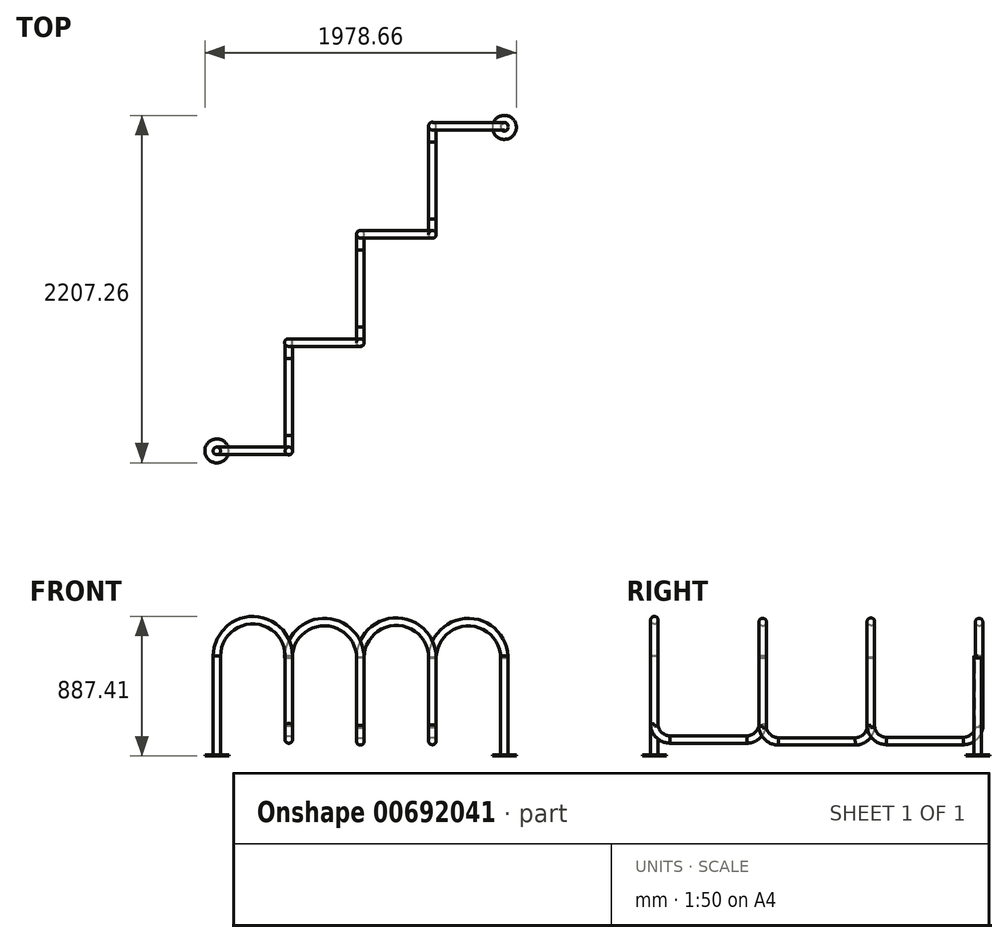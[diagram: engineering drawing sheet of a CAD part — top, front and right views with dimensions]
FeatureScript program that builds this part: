
annotation { "Feature Type Name" : "Feature", "Feature Type Description" : "" }
export const myFeature = defineFeature(function(context is Context, id is Id, definition is map)
    precondition{}
    {
        {
            var Q0;
            Q0=qCreatedBy(makeId("Top.planeOp"),FACE);
            var sketch = newSketch(context, id + "F0", { "sketchPlane" : qUnion([Q0])});
            skCircle(sketch, "E0", {"center": v(0, 0) * mm, "radius": 76.2 * mm});
            skCircle(sketch, "E1", {"center": v(0, 0) * mm, "radius": 23.81 * mm});
            skSolve(sketch);
        }
        {
            var Q0;
            Q0=makeQuery(id+"F0.imprint","IMPRINT",FACE,{"disambiguationData":[TD([[makeQuery(id+"F0.imprint","IMPRINT",EDGE,{"derivedFrom":sQuery(id+"F0.wireOp",EDGE,"E0")}),1.0]])]});
            extrude(context, id + "F1", {"entities" : qUnion([Q0]), "depth" : 6.35 * mm, "offsetDistance" : 25.4 * mm});
        }
        {
            var Q0;
            Q0=makeQuery(id+"F0.imprint","IMPRINT",FACE,{"disambiguationData":[TD([[makeQuery(id+"F0.imprint","IMPRINT",EDGE,{"derivedFrom":sQuery(id+"F0.wireOp",EDGE,"E1")}),1.0]])]});
            extrude(context, id + "F2", {"entities" : qUnion([Q0]), "operationType" : NewBodyOperationType.ADD, "depth" : 635 * mm, "offsetDistance" : 25.4 * mm});
        }
        {
            var Q0;
            Q0=qCreatedBy(makeId("Front.planeOp"),FACE);
            var sketch = newSketch(context, id + "F3", { "sketchPlane" : qUnion([Q0])});
            skArc(sketch, "E2", {"start": v(457.2, 635) * mm, "mid": v(228.6, 863.6) * mm, "end": v(0, 635) * mm});
            skLineSegment(sketch, "E3", {"start": v(0, 0) * mm, "end": v(0, 635) * mm});
            skLineSegment(sketch, "E4", {"start": v(457.2, 635) * mm, "end": v(457.2, 228.6) * mm});
            skLineSegment(sketch, "E5", {"start": v(228.6, 863.6) * mm, "end": v(228.6, 0) * mm, "construction": true});
            skLineSegment(sketch, "E6", {"start": v(228.6, 863.6) * mm, "end": v(951.54, 863.6) * mm, "construction": true});
            skSolve(sketch);
        }
        {
            var Q0;
            Q0=makeQuery(id+"F2.opExtrude","CAP_FACE",FACE,{"disambiguationData":[OSD([sQuery(id+"F0.wireOp",EDGE,"E1")])],"isStart":false});
            var Q1;
            Q1=sQuery(id+"F3.wireOp",EDGE,"E2");
            sweep(context, id + "F4", {"profiles" : qUnion([Q0]), "path" : qUnion([Q1])});
        }
        {
            var Q0;
            Q0=makeQuery(id+"F4.opSweep","CAP_FACE",FACE,{"disambiguationData":[OSD([sQuery(id+"F0.wireOp",EDGE,"E1"),sQuery(id+"F3.wireOp",VERTEX,"E2.start")])],"isStart":false});
            var sketch = newSketch(context, id + "F5", { "sketchPlane" : qUnion([Q0])});
            skCircle(sketch, "E7.0", {"center": v(457.2, 0) * mm, "radius": 23.81 * mm});
            skSolve(sketch);
        }
        {
            var Q0;
            Q0 = qSketchRegion(id + "F5", true);
            extrude(context, id + "F6", {"entities" : qUnion([Q0]), "operationType" : NewBodyOperationType.ADD, "depth" : 444.5 * mm, "offsetDistance" : 25.4 * mm});
        }
        {
            var Q0;
            Q0=qCreatedBy(makeId("Right.planeOp"),FACE);
            cPlane(context, id + "F7", {"entities" : qUnion([Q0]), "cplaneType" : CPlaneType.OFFSET, "offset" : 457.2 * mm, "width" : 152.4 * mm, "height" : 152.4 * mm});
        }
        {
            var Q0;
            Q0=qCreatedBy(id+"F7.planeOp",FACE);
            var sketch = newSketch(context, id + "F8", { "sketchPlane" : qUnion([Q0])});
            skLineSegment(sketch, "E8", {"start": v(100.01, 106.8) * mm, "end": v(587.38, 106.8) * mm});
            skArc(sketch, "E9", {"start": v(0, 203.2) * mm, "mid": v(30.96, 135.23) * mm, "end": v(100.01, 106.8) * mm});
            skArc(sketch, "E10", {"start": v(587.38, 106.8) * mm, "mid": v(656.43, 135.23) * mm, "end": v(687.39, 203.2) * mm});
            skLineSegment(sketch, "E11", {"start": v(687.39, 635) * mm, "end": v(687.52, 203.2) * mm});
            skLineSegment(sketch, "E12.0", {"start": v(23.81, 635) * mm, "end": v(-23.81, 635) * mm});
            skLineSegment(sketch, "E13", {"start": v(0, 635) * mm, "end": v(687.39, 635) * mm, "construction": true});
            skLineSegment(sketch, "E14", {"start": v(711.2, 203.2) * mm, "end": v(663.58, 203.2) * mm, "construction": true});
            skLineSegment(sketch, "E15.0", {"start": v(23.81, 203.2) * mm, "end": v(-23.81, 203.2) * mm});
            skSolve(sketch);
        }
        {
            var Q0;
            Q0=makeQuery(id+"F6.opExtrude","CAP_FACE",FACE,{"disambiguationData":[OSD([sQuery(id+"F5.wireOp",EDGE,"E7.0")])],"isStart":false});
            var Q1;
            Q1=sQuery(id+"F8.wireOp",EDGE,"E10");
            var Q2;
            Q2=sQuery(id+"F8.wireOp",EDGE,"E8");
            var Q3;
            Q3=sQuery(id+"F8.wireOp",EDGE,"E9");
            sweep(context, id + "F9", {"operationType" : NewBodyOperationType.ADD, "profiles" : qUnion([Q0]), "path" : qUnion([Q1, Q2, Q3])});
        }
        {
            var Q0;
            Q0=qCreatedBy(makeId("Top.planeOp"),FACE);
            var Q1;
            Q1=sQuery(id+"F8.wireOp",VERTEX,"E11.start");
            cPlane(context, id + "F10", {"entities" : qUnion([Q0, Q1]), "cplaneType" : CPlaneType.PLANE_POINT, "offset" : 25.4 * mm, "width" : 152.4 * mm, "height" : 152.4 * mm});
        }
        {
            var Q0;
            Q0=qCreatedBy(id+"F10.planeOp",FACE);
            var sketch = newSketch(context, id + "F11", { "sketchPlane" : qUnion([Q0])});
            skCircle(sketch, "E16", {"center": v(457.2, 687.39) * mm, "radius": 23.81 * mm});
            skSolve(sketch);
        }
        {
            var Q0;
            Q0=makeQuery(id+"F11.imprint","IMPRINT",FACE,{"disambiguationData":[TD([[makeQuery(id+"F11.imprint","IMPRINT",EDGE,{"derivedFrom":sQuery(id+"F11.wireOp",EDGE,"E16")}),1.0]])]});
            extrude(context, id + "F12", {"entities" : qUnion([Q0]), "operationType" : NewBodyOperationType.ADD, "oppositeDirection" : true, "depth" : 444.5 * mm, "offsetDistance" : 25.4 * mm});
        }
        {
            var Q0;
            Q0=makeQuery(id+"F4.opSweep","SWEPT_BODY",BODY,{"disambiguationData":[OSD([sQuery(id+"F0.wireOp",EDGE,"E1"),sQuery(id+"F3.wireOp",EDGE,"E2")])]});
            transform(context, id + "F13", {"entities" : qUnion([Q0]), "transformType" : TransformType.TRANSLATION_3D, "dx" : 454.4 * mm, "dy" : 688.34 * mm, "dz" : -11.94 * mm, "makeCopy" : true});
        }
        {
            var Q0;
            Q0=makeQuery(id+"F13.opPattern","COPY",BODY,{"derivedFrom":makeQuery(id+"F4.opSweep","SWEPT_BODY",BODY,{"disambiguationData":[OSD([sQuery(id+"F0.wireOp",EDGE,"E1"),sQuery(id+"F3.wireOp",EDGE,"E2")])]}),"instanceName":"1"});
            transform(context, id + "F14", {"entities" : qUnion([Q0]), "transformType" : TransformType.TRANSLATION_3D, "dx" : 457.2 * mm, "dy" : 687.4 * mm, "dz" : 2.54 * mm, "makeCopy" : true});
        }
        {
            var Q0;
            Q0=qCreatedBy(makeId("Front.planeOp"),FACE);
            cPlane(context, id + "F15", {"entities" : qUnion([Q0]), "cplaneType" : CPlaneType.OFFSET, "offset" : 685.8 * mm, "width" : 152.4 * mm, "height" : 152.4 * mm});
        }
        {
            var Q0;
            Q0=qCreatedBy(id+"F15.planeOp",FACE);
            var sketch = newSketch(context, id + "F16", { "sketchPlane" : qUnion([Q0])});
            skArc(sketch, "E17.0", {"start": v(457.2, 635) * mm, "mid": v(228.6, 863.6) * mm, "end": v(0, 635) * mm});
            skLineSegment(sketch, "E18.0", {"start": v(-23.81, 635) * mm, "end": v(23.81, 635) * mm});
            skSolve(sketch);
        }
        {
            var Q0;
            Q0=qCreatedBy(makeId("Top.planeOp"),FACE);
            cPlane(context, id + "F17", {"entities" : qUnion([Q0]), "cplaneType" : CPlaneType.OFFSET, "offset" : 635 * mm, "width" : 152.4 * mm, "height" : 152.4 * mm});
        }
        {
            var Q0;
            Q0=qCreatedBy(id+"F17.planeOp",FACE);
            var sketch = newSketch(context, id + "F18", { "sketchPlane" : qUnion([Q0])});
            skLineSegment(sketch, "E19.0", {"start": v(-23.81, -685.8) * mm, "end": v(23.81, -685.8) * mm});
            skCircle(sketch, "E20", {"center": v(0, -685.8) * mm, "radius": 23.81 * mm});
            skSolve(sketch);
        }
        {
            var Q0;
            {var subQ0=sQuery(id+"F18.wireOp",EDGE,"E19.0");Q0=makeQuery(id+"F18.imprint","IMPRINT",FACE,{"disambiguationData":[TD([[makeQuery(id+"F18.imprint","IMPRINT",EDGE,{"derivedFrom":subQ0}),-1.0]])]});}
            var Q1;
            {var subQ0=sQuery(id+"F18.wireOp",EDGE,"E19.0");Q1=makeQuery(id+"F18.imprint","IMPRINT",FACE,{"disambiguationData":[TD([[makeQuery(id+"F18.imprint","IMPRINT",EDGE,{"derivedFrom":subQ0}),1.0]])]});}
            var Q2;
            Q2=sQuery(id+"F16.wireOp",EDGE,"E17.0");
            sweep(context, id + "F19", {"profiles" : qUnion([Q0, Q1]), "path" : qUnion([Q2])});
        }
        {
            var Q0;
            Q0=makeQuery(id+"F19.opSweep","SWEPT_BODY",BODY,{"disambiguationData":[OSD([sQuery(id+"F16.wireOp",EDGE,"E17.0"),sQuery(id+"F18.wireOp",EDGE,"E20")])]});
            transform(context, id + "F20", {"entities" : qUnion([Q0]), "transformType" : TransformType.TRANSLATION_3D, "dx" : 1369.06 * mm, "dy" : 2748.28 * mm, "dz" : -12.7 * mm, "makeCopy" : false});
        }
        {
            var Q0;
            Q0=makeQuery(id+"F1.opExtrude","SWEPT_BODY",BODY,{"disambiguationData":[OSD([sQuery(id+"F0.wireOp",EDGE,"E0"),sQuery(id+"F0.wireOp",EDGE,"E1")])]});
            transform(context, id + "F21", {"entities" : qUnion([Q0]), "transformType" : TransformType.TRANSLATION_3D, "dx" : 1826.26 * mm, "dy" : 2054.86 * mm, "dz" : 0 * mm, "makeCopy" : true});
        }
    });
